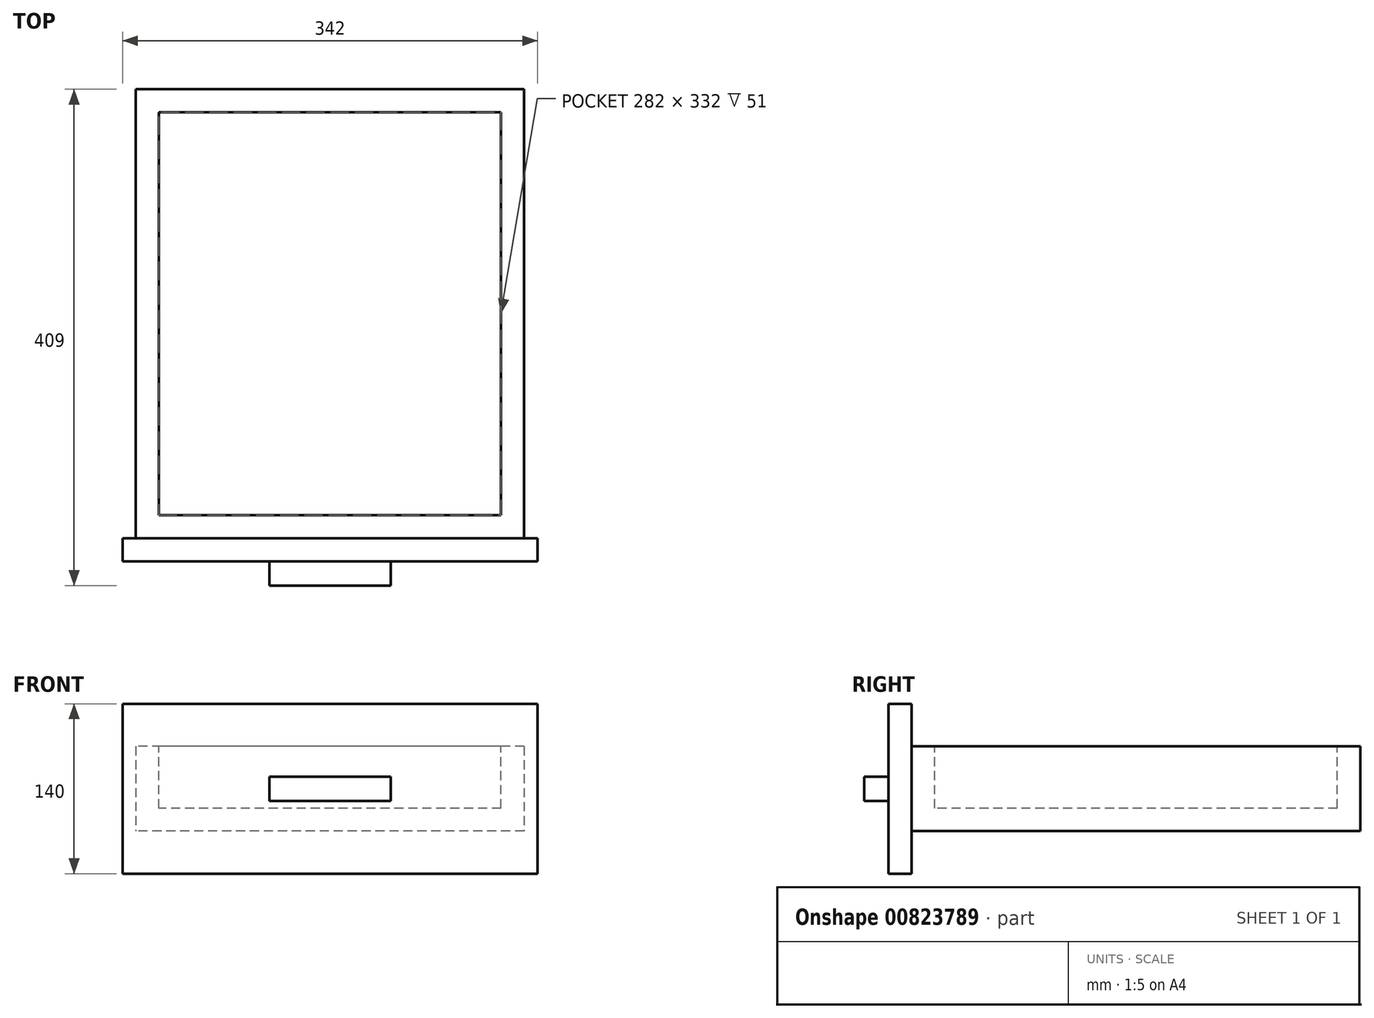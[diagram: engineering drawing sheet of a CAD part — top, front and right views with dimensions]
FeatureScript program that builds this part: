
annotation { "Feature Type Name" : "Feature", "Feature Type Description" : "" }
export const myFeature = defineFeature(function(context is Context, id is Id, definition is map)
    precondition{}
    {
        {
            var Q0;
            Q0=qCreatedBy(makeId("Top.planeOp"),FACE);
            var sketch = newSketch(context, id + "F0", { "sketchPlane" : qUnion([Q0])});
            skLineSegment(sketch, "E0.bottom", {"start": v(160, -185) * mm, "end": v(-160, -185) * mm});
            skLineSegment(sketch, "E0.top", {"start": v(160, 185) * mm, "end": v(-160, 185) * mm});
            skLineSegment(sketch, "E0.left", {"start": v(160, -185) * mm, "end": v(160, 185) * mm});
            skLineSegment(sketch, "E0.right", {"start": v(-160, -185) * mm, "end": v(-160, 185) * mm});
            skPoint(sketch, "E0.middle", {"position": v(0, 0) * mm});
            skSolve(sketch);
        }
        {
            var Q0;
            Q0=makeQuery(id+"F0.imprint","IMPRINT",FACE,{"disambiguationData":[TD([[makeQuery(id+"F0.imprint","IMPRINT",EDGE,{"derivedFrom":sQuery(id+"F0.wireOp",EDGE,"E0.bottom")}),-1.0]])]});
            extrude(context, id + "F1", {"entities" : qUnion([Q0]), "depth" : 70 * mm, "offsetDistance" : 25 * mm});
        }
        {
            var Q0;
            Q0=makeQuery(id+"F1.opExtrude","CAP_FACE",FACE,{"disambiguationData":[OSD([sQuery(id+"F0.wireOp",EDGE,"E0.bottom"),sQuery(id+"F0.wireOp",EDGE,"E0.top"),sQuery(id+"F0.wireOp",EDGE,"E0.left"),sQuery(id+"F0.wireOp",EDGE,"E0.right")])],"isStart":false});
            var sketch = newSketch(context, id + "F2", { "sketchPlane" : qUnion([Q0])});
            skLineSegment(sketch, "E1.bottom", {"start": v(141, 166) * mm, "end": v(-141, 166) * mm});
            skLineSegment(sketch, "E1.top", {"start": v(141, -166) * mm, "end": v(-141, -166) * mm});
            skLineSegment(sketch, "E1.left", {"start": v(141, 166) * mm, "end": v(141, -166) * mm});
            skLineSegment(sketch, "E1.right", {"start": v(-141, 166) * mm, "end": v(-141, -166) * mm});
            skPoint(sketch, "E1.middle", {"position": v(0, 0) * mm});
            skSolve(sketch);
        }
        {
            var Q0;
            Q0=makeQuery(id+"F2.imprint","IMPRINT",FACE,{"disambiguationData":[TD([[makeQuery(id+"F2.imprint","IMPRINT",EDGE,{"derivedFrom":sQuery(id+"F2.wireOp",EDGE,"E1.bottom")}),1.0]])]});
            extrude(context, id + "F3", {"entities" : qUnion([Q0]), "operationType" : NewBodyOperationType.REMOVE, "oppositeDirection" : true, "depth" : 51 * mm, "offsetDistance" : 25 * mm});
        }
        {
            var Q0;
            Q0=makeQuery(id+"F1.opExtrude","SWEPT_FACE",FACE,{"disambiguationData":[OSD([sQuery(id+"F0.wireOp",EDGE,"E0.bottom")])]});
            var sketch = newSketch(context, id + "F4", { "sketchPlane" : qUnion([Q0])});
            skLineSegment(sketch, "E2.bottom", {"start": v(171, -35) * mm, "end": v(-171, -35) * mm});
            skLineSegment(sketch, "E2.top", {"start": v(171, 105) * mm, "end": v(-171, 105) * mm});
            skLineSegment(sketch, "E2.left", {"start": v(171, -35) * mm, "end": v(171, 105) * mm});
            skLineSegment(sketch, "E2.right", {"start": v(-171, -35) * mm, "end": v(-171, 105) * mm});
            skPoint(sketch, "E2.middle", {"position": v(0, 35) * mm});
            skPoint(sketch, "E2.middle.positionSnap0", {"position": v(-160, 35) * mm});
            skPoint(sketch, "E2.centerSnap0", {"position": v(-160, 35) * mm});
            skSolve(sketch);
        }
        {
            var Q0;
            {var subQ0=sQuery(id+"F0.wireOp",EDGE,"E0.bottom");Q0=makeQuery(id+"F4.imprint","IMPRINT",FACE,{"disambiguationData":[TD([[makeQuery(id+"F4.imprint","IMPRINT",EDGE,{"derivedFrom":makeQuery(id+"F1.opExtrude","CAP_EDGE",EDGE,{"disambiguationData":[OSD([subQ0])],"isStart":true})}),-1.0]])]});}
            var Q1;
            Q1=makeQuery(id+"F4.imprint","IMPRINT",FACE,{"disambiguationData":[TD([[makeQuery(id+"F4.imprint","IMPRINT",EDGE,{"derivedFrom":sQuery(id+"F4.wireOp",EDGE,"E2.bottom")}),-1.0]])]});
            extrude(context, id + "F5", {"entities" : qUnion([Q0, Q1]), "operationType" : NewBodyOperationType.ADD, "depth" : 19 * mm, "offsetDistance" : 25 * mm});
        }
        {
            var Q0;
            Q0=makeQuery(id+"F5.opExtrude","CAP_FACE",FACE,{"disambiguationData":[OSD([sQuery(id+"F4.wireOp",EDGE,"E2.bottom"),sQuery(id+"F4.wireOp",EDGE,"E2.top"),sQuery(id+"F4.wireOp",EDGE,"E2.left"),sQuery(id+"F4.wireOp",EDGE,"E2.right")])],"isStart":false});
            var sketch = newSketch(context, id + "F6", { "sketchPlane" : qUnion([Q0])});
            skLineSegment(sketch, "E3.bottom", {"start": v(-50, 25) * mm, "end": v(50, 25) * mm});
            skLineSegment(sketch, "E3.top", {"start": v(-50, 45) * mm, "end": v(50, 45) * mm});
            skLineSegment(sketch, "E3.left", {"start": v(-50, 25) * mm, "end": v(-50, 45) * mm});
            skLineSegment(sketch, "E3.right", {"start": v(50, 25) * mm, "end": v(50, 45) * mm});
            skPoint(sketch, "E3.middle", {"position": v(0, 35) * mm});
            skPoint(sketch, "E3.middle.positionSnap0", {"position": v(-171, 35) * mm});
            skPoint(sketch, "E3.centerSnap0", {"position": v(-171, 35) * mm});
            skSolve(sketch);
        }
        {
            var Q0;
            Q0=makeQuery(id+"F6.imprint","IMPRINT",FACE,{"disambiguationData":[TD([[makeQuery(id+"F6.imprint","IMPRINT",EDGE,{"derivedFrom":sQuery(id+"F6.wireOp",EDGE,"E3.bottom")}),1.0]])]});
            extrude(context, id + "F7", {"entities" : qUnion([Q0]), "operationType" : NewBodyOperationType.ADD, "depth" : 20 * mm, "offsetDistance" : 25 * mm});
        }
    });
